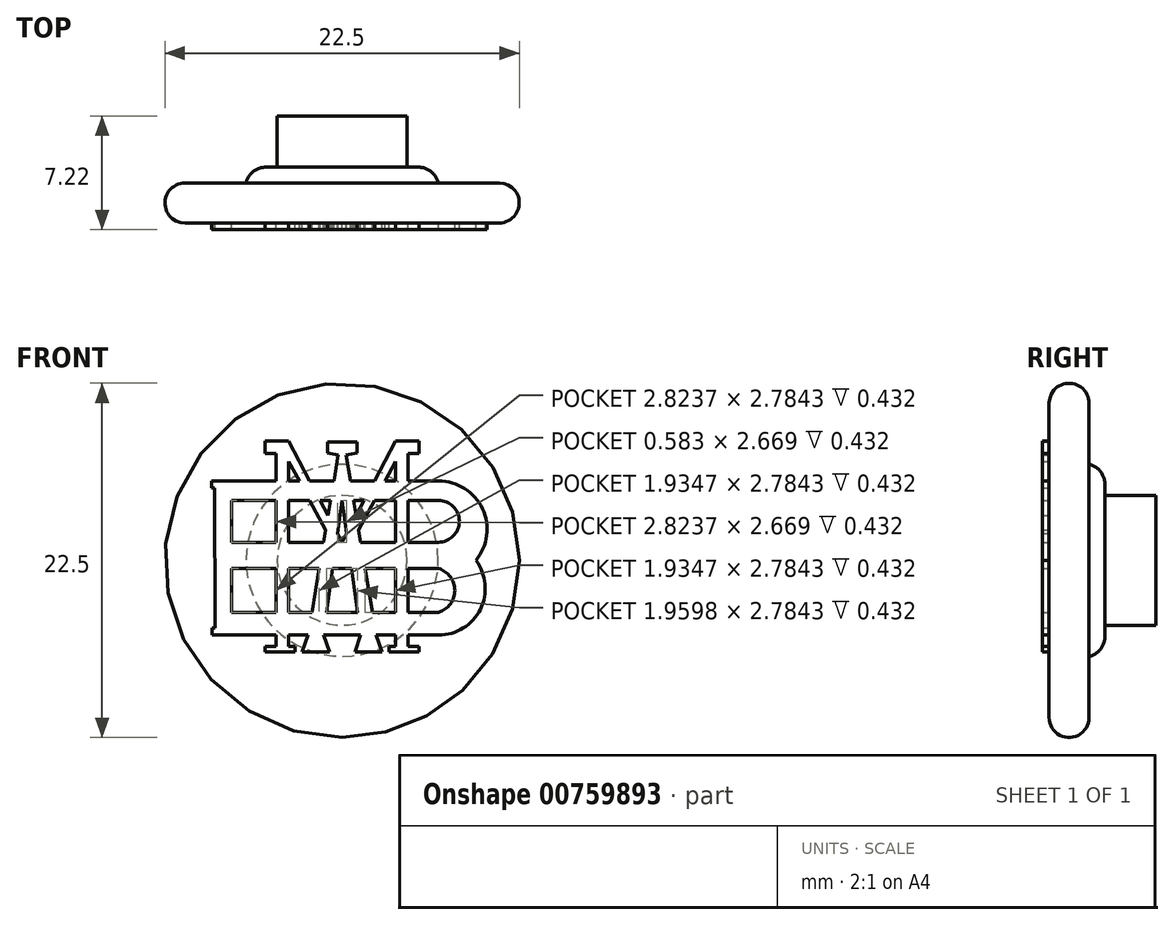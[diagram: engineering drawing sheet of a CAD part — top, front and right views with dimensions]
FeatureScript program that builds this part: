
annotation { "Feature Type Name" : "Feature", "Feature Type Description" : "" }
export const myFeature = defineFeature(function(context is Context, id is Id, definition is map)
    precondition{}
    {
        {
            var Q0;
            Q0=qCreatedBy(makeId("Front.planeOp"),FACE);
            var sketch = newSketch(context, id + "F0", { "sketchPlane" : qUnion([Q0])});
            skCircle(sketch, "E0", {"center": v(0, 0) * mm, "radius": 4.12 * mm});
            skCircle(sketch, "E1", {"center": v(0, 0) * mm, "radius": 11.25 * mm});
            skCircle(sketch, "E2", {"center": v(0, 0) * mm, "radius": 6.1 * mm});
            skSolve(sketch);
        }
        {
            var Q0;
            Q0=makeQuery(id+"F0.imprint","IMPRINT",FACE,{"disambiguationData":[TD([[makeQuery(id+"F0.imprint","IMPRINT",EDGE,{"derivedFrom":sQuery(id+"F0.wireOp",EDGE,"E1")}),1.0]])]});
            var Q1;
            Q1=makeQuery(id+"F0.imprint","IMPRINT",FACE,{"disambiguationData":[TD([[makeQuery(id+"F0.imprint","IMPRINT",EDGE,{"derivedFrom":sQuery(id+"F0.wireOp",EDGE,"E0")}),1.0]])]});
            var Q2;
            Q2=makeQuery(id+"F0.imprint","IMPRINT",FACE,{"disambiguationData":[TD([[makeQuery(id+"F0.imprint","IMPRINT",EDGE,{"derivedFrom":sQuery(id+"F0.wireOp",EDGE,"E0")}),-1.0]])]});
            extrude(context, id + "F1", {"entities" : qUnion([Q0, Q1, Q2]), "depth" : 2.54 * mm, "offsetDistance" : 25.4 * mm});
        }
        {
            var Q0;
            Q0=makeQuery(id+"F0.imprint","IMPRINT",FACE,{"disambiguationData":[TD([[makeQuery(id+"F0.imprint","IMPRINT",EDGE,{"derivedFrom":sQuery(id+"F0.wireOp",EDGE,"E0")}),1.0]])]});
            extrude(context, id + "F2", {"entities" : qUnion([Q0]), "operationType" : NewBodyOperationType.ADD, "oppositeDirection" : true, "depth" : 4.25 * mm, "offsetDistance" : 25.4 * mm});
        }
        {
            var Q0;
            Q0=makeQuery(id+"F0.imprint","IMPRINT",FACE,{"disambiguationData":[TD([[makeQuery(id+"F0.imprint","IMPRINT",EDGE,{"derivedFrom":sQuery(id+"F0.wireOp",EDGE,"E0")}),-1.0]])]});
            extrude(context, id + "F3", {"entities" : qUnion([Q0]), "operationType" : NewBodyOperationType.ADD, "oppositeDirection" : true, "depth" : 1 * mm, "offsetDistance" : 25.4 * mm});
        }
        {
            var Q0;
            Q0=makeQuery(id+"F3.opExtrude","CAP_EDGE",EDGE,{"disambiguationData":[OSD([sQuery(id+"F0.wireOp",EDGE,"E2")])],"isStart":false});
            var Q1;
            Q1=makeQuery(id+"F1.opExtrude","CAP_EDGE",EDGE,{"disambiguationData":[OSD([sQuery(id+"F0.wireOp",EDGE,"E1")])],"isStart":true});
            var Q2;
            Q2=makeQuery(id+"F1.opExtrude","CAP_EDGE",EDGE,{"disambiguationData":[OSD([sQuery(id+"F0.wireOp",EDGE,"E1")])],"isStart":false});
            fillet(context, id + "F4", {"entities" : qUnion([Q0, Q1, Q2]), "radius" : 1.27 * mm, "tangentPropagation" : true, "allowEdgeOverflow" : false});
        }
        {
            var Q0;
            Q0=makeQuery(id+"F1.opExtrude","CAP_FACE",FACE,{"disambiguationData":[OSD([sQuery(id+"F0.wireOp",EDGE,"E1")])],"isStart":false});
            var sketch = newSketch(context, id + "F5", { "sketchPlane" : qUnion([Q0])});
            skArc(sketch, "E3", {"start": v(6.13, 1.14) * mm, "mid": v(7.44, 2.48) * mm, "end": v(6.13, 3.81) * mm});
            skArc(sketch, "E4", {"start": v(6.13, -3.3) * mm, "mid": v(7.15, -1.9) * mm, "end": v(6.13, -0.52) * mm});
            skArc(sketch, "E5", {"start": v(6.13, -4.75) * mm, "mid": v(8.78, -3.1) * mm, "end": v(8.5, 0) * mm});
            skArc(sketch, "E6", {"start": v(8.5, 0) * mm, "mid": v(8.91, 3.27) * mm, "end": v(6.13, 5.04) * mm});
            skLineSegment(sketch, "E7", {"start": v(-2.17, -4.75) * mm, "end": v(-2.54, -5.8) * mm});
            skLineSegment(sketch, "E8", {"start": v(-2.17, -4.75) * mm, "end": v(-0.24, 6.7) * mm});
            skPoint(sketch, "E8.endSnap0", {"position": v(-0.24, 1.14) * mm});
            skLineSegment(sketch, "E9.MirrorCS", {"start": v(2.17, -4.75) * mm, "end": v(0.24, 6.7) * mm});
            skLineSegment(sketch, "E10.MirrorCS", {"start": v(2.17, -4.75) * mm, "end": v(2.54, -5.8) * mm});
            skLineSegment(sketch, "E11", {"start": v(-2.54, -5.8) * mm, "end": v(-0.8, -5.8) * mm});
            skLineSegment(sketch, "E12", {"start": v(-0.8, -5.8) * mm, "end": v(-1.18, -4.75) * mm});
            skLineSegment(sketch, "E13", {"start": v(-0.24, 6.7) * mm, "end": v(-0.93, 6.8) * mm});
            skLineSegment(sketch, "E14", {"start": v(-0.93, 6.8) * mm, "end": v(-0.93, 7.52) * mm});
            skLineSegment(sketch, "E15", {"start": v(-0.93, 7.52) * mm, "end": v(0, 7.52) * mm});
            skLineSegment(sketch, "E16.MirrorCS", {"start": v(0.93, 7.52) * mm, "end": v(0, 7.52) * mm});
            skLineSegment(sketch, "E17.MirrorCS", {"start": v(0.93, 6.8) * mm, "end": v(0.93, 7.52) * mm});
            skLineSegment(sketch, "E18.MirrorCS", {"start": v(0.24, 6.7) * mm, "end": v(0.93, 6.8) * mm});
            skLineSegment(sketch, "E19.MirrorCS", {"start": v(0.8, -5.8) * mm, "end": v(1.18, -4.75) * mm});
            skLineSegment(sketch, "E20.MirrorCS", {"start": v(2.54, -5.8) * mm, "end": v(0.8, -5.8) * mm});
            skLineSegment(sketch, "E21", {"start": v(1.18, -4.75) * mm, "end": v(0, 3.81) * mm});
            skLineSegment(sketch, "E22", {"start": v(-1.18, -4.75) * mm, "end": v(0, 3.81) * mm});
            skLineSegment(sketch, "E23", {"start": v(-4.19, -4.75) * mm, "end": v(-4.19, -5.45) * mm});
            skLineSegment(sketch, "E24", {"start": v(-3.4, -4.75) * mm, "end": v(-3.4, -5.45) * mm});
            skLineSegment(sketch, "E25", {"start": v(-4.19, -4.75) * mm, "end": v(-4.19, 6.79) * mm});
            skLineSegment(sketch, "E26", {"start": v(-4.19, 6.79) * mm, "end": v(-4.88, 6.79) * mm});
            skLineSegment(sketch, "E27", {"start": v(-4.88, 7.58) * mm, "end": v(-3.4, 7.58) * mm});
            skLineSegment(sketch, "E28", {"start": v(-4.88, 7.58) * mm, "end": v(-4.88, 6.79) * mm});
            skLineSegment(sketch, "E29", {"start": v(-3.4, 7.58) * mm, "end": v(0, 1.14) * mm});
            skLineSegment(sketch, "E30", {"start": v(-4.19, -5.45) * mm, "end": v(-4.88, -5.45) * mm});
            skLineSegment(sketch, "E31", {"start": v(-4.88, -5.45) * mm, "end": v(-4.88, -5.8) * mm});
            skLineSegment(sketch, "E32", {"start": v(-4.88, -5.8) * mm, "end": v(-2.98, -5.8) * mm});
            skLineSegment(sketch, "E33", {"start": v(-3.4, -5.45) * mm, "end": v(-2.98, -5.45) * mm});
            skLineSegment(sketch, "E34", {"start": v(-2.98, -5.45) * mm, "end": v(-2.98, -5.8) * mm});
            skLineSegment(sketch, "E35.MirrorCS", {"start": v(3.4, 7.58) * mm, "end": v(0, 1.14) * mm});
            skLineSegment(sketch, "E36.MirrorCS", {"start": v(4.88, 7.58) * mm, "end": v(3.4, 7.58) * mm});
            skLineSegment(sketch, "E37.MirrorCS", {"start": v(4.88, 7.58) * mm, "end": v(4.88, 6.79) * mm});
            skLineSegment(sketch, "E38.MirrorCS", {"start": v(4.19, 6.79) * mm, "end": v(4.88, 6.79) * mm});
            skLineSegment(sketch, "E39.MirrorCS", {"start": v(4.19, -4.75) * mm, "end": v(4.19, 6.79) * mm});
            skLineSegment(sketch, "E40.MirrorCS", {"start": v(4.88, -5.45) * mm, "end": v(4.88, -5.8) * mm});
            skLineSegment(sketch, "E41.MirrorCS", {"start": v(4.19, -5.45) * mm, "end": v(4.88, -5.45) * mm});
            skLineSegment(sketch, "E42.MirrorCS", {"start": v(3.4, -5.45) * mm, "end": v(2.98, -5.45) * mm});
            skLineSegment(sketch, "E43.MirrorCS", {"start": v(2.98, -5.45) * mm, "end": v(2.98, -5.8) * mm});
            skLineSegment(sketch, "E44.MirrorCS", {"start": v(4.88, -5.8) * mm, "end": v(2.98, -5.8) * mm});
            skLineSegment(sketch, "E45.MirrorCS", {"start": v(3.4, -4.75) * mm, "end": v(3.4, -5.45) * mm});
            skLineSegment(sketch, "E46.MirrorCS", {"start": v(4.19, -4.75) * mm, "end": v(4.19, -5.45) * mm});
            skLineSegment(sketch, "E47", {"start": v(-3.4, -4.75) * mm, "end": v(-3.4, 6.3) * mm});
            skLineSegment(sketch, "E48", {"start": v(-3.4, 6.3) * mm, "end": v(0, 0) * mm});
            skLineSegment(sketch, "E49.MirrorCS", {"start": v(3.4, 6.3) * mm, "end": v(0, 0) * mm});
            skLineSegment(sketch, "E50.MirrorCS", {"start": v(3.4, -4.75) * mm, "end": v(3.4, 6.3) * mm});
            skLineSegment(sketch, "E51", {"start": v(6.13, 5.04) * mm, "end": v(5.18, 5.04) * mm});
            skLineSegment(sketch, "E52", {"start": v(-7.71, 5.04) * mm, "end": v(5.18, 5.04) * mm});
            skLineSegment(sketch, "E53", {"start": v(6.13, -4.75) * mm, "end": v(-7.71, -4.75) * mm});
            skLineSegment(sketch, "E54", {"start": v(-7.71, 5.04) * mm, "end": v(-8.3, 5.04) * mm});
            skLineSegment(sketch, "E55", {"start": v(-8.3, 5.04) * mm, "end": v(-8.3, 4.59) * mm});
            skLineSegment(sketch, "E56", {"start": v(-8.3, 4.59) * mm, "end": v(-8.1, 4.59) * mm});
            skLineSegment(sketch, "E57", {"start": v(6.13, 3.81) * mm, "end": v(-7.01, 3.81) * mm});
            skLineSegment(sketch, "E58", {"start": v(6.13, 1.14) * mm, "end": v(-7.01, 1.14) * mm});
            skLineSegment(sketch, "E59", {"start": v(6.13, -0.52) * mm, "end": v(-7.01, -0.52) * mm});
            skLineSegment(sketch, "E60", {"start": v(6.13, -3.3) * mm, "end": v(-7.01, -3.3) * mm});
            skLineSegment(sketch, "E61", {"start": v(-7.01, -3.3) * mm, "end": v(-7.01, 3.81) * mm});
            skLineSegment(sketch, "E62", {"start": v(8.5, 0) * mm, "end": v(-8.1, 0) * mm});
            skLineSegment(sketch, "E63.MirrorCS", {"start": v(-7.68, -4.75) * mm, "end": v(-8.27, -4.75) * mm});
            skLineSegment(sketch, "E64", {"start": v(-8.27, -4.3) * mm, "end": v(-8.27, -4.75) * mm});
            skLineSegment(sketch, "E65", {"start": v(-8.27, -4.3) * mm, "end": v(-8.08, -4.3) * mm});
            skLineSegment(sketch, "E66", {"start": v(-8.1, 4.59) * mm, "end": v(-8.08, -4.3) * mm});
            skSolve(sketch);
        }
        {
            var Q0;
            {var subQ0=sQuery(id+"F5.wireOp",EDGE,"E59");var subQ1=sQuery(id+"F5.wireOp",EDGE,"E25");var subQ2=makeQuery(id+"F5.imprint","INTERSECT",VERTEX,{"derivedFrom":[subQ1,subQ0]});Q0=makeQuery(id+"F5.imprint","IMPRINT",FACE,{"disambiguationData":[TD([[makeQuery(id+"F5.imprint","IMPRINT",EDGE,{"disambiguationData":[TD([[subQ2,-1.0]])],"derivedFrom":subQ1}),1.0]])]});}
            var Q1;
            {var subQ1=sQuery(id+"F5.wireOp",EDGE,"E26");Q1=makeQuery(id+"F5.imprint","IMPRINT",FACE,{"disambiguationData":[TD([[makeQuery(id+"F5.imprint","IMPRINT",EDGE,{"derivedFrom":subQ1}),-1.0]])]});}
            var Q2;
            {var subQ0=sQuery(id+"F5.wireOp",EDGE,"E58");var subQ1=sQuery(id+"F5.wireOp",EDGE,"E22");var subQ2=makeQuery(id+"F5.imprint","INTERSECT",VERTEX,{"derivedFrom":[subQ1,subQ0]});Q2=makeQuery(id+"F5.imprint","IMPRINT",FACE,{"disambiguationData":[TD([[makeQuery(id+"F5.imprint","IMPRINT",EDGE,{"disambiguationData":[TD([[subQ2,-1.0]])],"derivedFrom":subQ1}),-1.0]])]});}
            var Q3;
            {var subQ1=sQuery(id+"F5.wireOp",EDGE,"E36.MirrorCS");Q3=makeQuery(id+"F5.imprint","IMPRINT",FACE,{"disambiguationData":[TD([[makeQuery(id+"F5.imprint","IMPRINT",EDGE,{"derivedFrom":subQ1}),1.0]])]});}
            var Q4;
            {var subQ0=sQuery(id+"F5.wireOp",EDGE,"E13");Q4=makeQuery(id+"F5.imprint","IMPRINT",FACE,{"disambiguationData":[TD([[makeQuery(id+"F5.imprint","IMPRINT",EDGE,{"derivedFrom":subQ0}),-1.0]])]});}
            var Q5;
            {var subQ0=sQuery(id+"F5.wireOp",EDGE,"E58");var subQ1=sQuery(id+"F5.wireOp",EDGE,"E9.MirrorCS");var subQ2=makeQuery(id+"F5.imprint","INTERSECT",VERTEX,{"derivedFrom":[subQ1,subQ0]});Q5=makeQuery(id+"F5.imprint","IMPRINT",FACE,{"disambiguationData":[TD([[makeQuery(id+"F5.imprint","IMPRINT",EDGE,{"disambiguationData":[TD([[subQ2,-1.0]])],"derivedFrom":subQ1}),1.0]])]});}
            var Q6;
            {var subQ0=sQuery(id+"F5.wireOp",EDGE,"E58");var subQ1=sQuery(id+"F5.wireOp",EDGE,"E21");var subQ2=makeQuery(id+"F5.imprint","INTERSECT",VERTEX,{"derivedFrom":[subQ1,subQ0]});Q6=makeQuery(id+"F5.imprint","IMPRINT",FACE,{"disambiguationData":[TD([[makeQuery(id+"F5.imprint","IMPRINT",EDGE,{"disambiguationData":[TD([[subQ2,-1.0]])],"derivedFrom":subQ1}),1.0]])]});}
            var Q7;
            {var subQ14=sQuery(id+"F5.wireOp",EDGE,"E3");Q7=makeQuery(id+"F5.imprint","IMPRINT",FACE,{"disambiguationData":[TD([[makeQuery(id+"F5.imprint","IMPRINT",EDGE,{"derivedFrom":subQ14}),-1.0]])]});}
            var Q8;
            {var subQ1=sQuery(id+"F5.wireOp",EDGE,"E23");Q8=makeQuery(id+"F5.imprint","IMPRINT",FACE,{"disambiguationData":[TD([[makeQuery(id+"F5.imprint","IMPRINT",EDGE,{"derivedFrom":subQ1}),1.0]])]});}
            var Q9;
            {var subQ0=sQuery(id+"F5.wireOp",EDGE,"E7");Q9=makeQuery(id+"F5.imprint","IMPRINT",FACE,{"disambiguationData":[TD([[makeQuery(id+"F5.imprint","IMPRINT",EDGE,{"derivedFrom":subQ0}),1.0]])]});}
            var Q10;
            {var subQ0=sQuery(id+"F5.wireOp",EDGE,"E10.MirrorCS");Q10=makeQuery(id+"F5.imprint","IMPRINT",FACE,{"disambiguationData":[TD([[makeQuery(id+"F5.imprint","IMPRINT",EDGE,{"derivedFrom":subQ0}),-1.0]])]});}
            var Q11;
            Q11=makeQuery(id+"F5.imprint","IMPRINT",FACE,{"disambiguationData":[TD([[makeQuery(id+"F5.imprint","IMPRINT",EDGE,{"derivedFrom":sQuery(id+"F5.wireOp",EDGE,"E40.MirrorCS")}),-1.0]])]});
            var Q12;
            {var subQ0=sQuery(id+"F5.wireOp",EDGE,"E60");var subQ1=sQuery(id+"F5.wireOp",EDGE,"E25");var subQ2=makeQuery(id+"F5.imprint","INTERSECT",VERTEX,{"derivedFrom":[subQ1,subQ0]});Q12=makeQuery(id+"F5.imprint","IMPRINT",FACE,{"disambiguationData":[TD([[makeQuery(id+"F5.imprint","IMPRINT",EDGE,{"disambiguationData":[TD([[subQ2,-1.0]])],"derivedFrom":subQ1}),-1.0]])]});}
            var Q13;
            {var subQ0=sQuery(id+"F5.wireOp",EDGE,"E59");var subQ1=sQuery(id+"F5.wireOp",EDGE,"E25");var subQ2=makeQuery(id+"F5.imprint","INTERSECT",VERTEX,{"derivedFrom":[subQ1,subQ0]});Q13=makeQuery(id+"F5.imprint","IMPRINT",FACE,{"disambiguationData":[TD([[makeQuery(id+"F5.imprint","IMPRINT",EDGE,{"disambiguationData":[TD([[subQ2,-1.0]])],"derivedFrom":subQ1}),-1.0]])]});}
            var Q14;
            {var subQ0=sQuery(id+"F5.wireOp",EDGE,"E58");var subQ1=sQuery(id+"F5.wireOp",EDGE,"E25");var subQ2=makeQuery(id+"F5.imprint","INTERSECT",VERTEX,{"derivedFrom":[subQ1,subQ0]});Q14=makeQuery(id+"F5.imprint","IMPRINT",FACE,{"disambiguationData":[TD([[makeQuery(id+"F5.imprint","IMPRINT",EDGE,{"disambiguationData":[TD([[subQ2,-1.0]])],"derivedFrom":subQ1}),-1.0]])]});}
            var Q15;
            {var subQ0=sQuery(id+"F5.wireOp",EDGE,"E57");var subQ1=sQuery(id+"F5.wireOp",EDGE,"E25");var subQ2=makeQuery(id+"F5.imprint","INTERSECT",VERTEX,{"derivedFrom":[subQ1,subQ0]});Q15=makeQuery(id+"F5.imprint","IMPRINT",FACE,{"disambiguationData":[TD([[makeQuery(id+"F5.imprint","IMPRINT",EDGE,{"disambiguationData":[TD([[subQ2,-1.0]])],"derivedFrom":subQ1}),-1.0]])]});}
            var Q16;
            {var subQ0=sQuery(id+"F5.wireOp",EDGE,"E48");var subQ1=sQuery(id+"F5.wireOp",EDGE,"E8");var subQ2=makeQuery(id+"F5.imprint","INTERSECT",VERTEX,{"derivedFrom":[subQ1,subQ0]});Q16=makeQuery(id+"F5.imprint","IMPRINT",FACE,{"disambiguationData":[TD([[makeQuery(id+"F5.imprint","IMPRINT",EDGE,{"disambiguationData":[TD([[subQ2,-1.0]])],"derivedFrom":subQ1}),-1.0]])]});}
            var Q17;
            {var subQ0=sQuery(id+"F5.wireOp",EDGE,"E48");var subQ1=sQuery(id+"F5.wireOp",EDGE,"E8");var subQ2=makeQuery(id+"F5.imprint","INTERSECT",VERTEX,{"derivedFrom":[subQ1,subQ0]});Q17=makeQuery(id+"F5.imprint","IMPRINT",FACE,{"disambiguationData":[TD([[makeQuery(id+"F5.imprint","IMPRINT",EDGE,{"disambiguationData":[TD([[subQ2,-1.0]])],"derivedFrom":subQ1}),1.0]])]});}
            var Q18;
            {var subQ0=sQuery(id+"F5.wireOp",EDGE,"E29");var subQ1=sQuery(id+"F5.wireOp",EDGE,"E8");var subQ2=makeQuery(id+"F5.imprint","INTERSECT",VERTEX,{"derivedFrom":[subQ1,subQ0]});Q18=makeQuery(id+"F5.imprint","IMPRINT",FACE,{"disambiguationData":[TD([[makeQuery(id+"F5.imprint","IMPRINT",EDGE,{"disambiguationData":[TD([[subQ2,-1.0]])],"derivedFrom":subQ1}),-1.0]])]});}
            var Q19;
            {var subQ0=sQuery(id+"F5.wireOp",EDGE,"E35.MirrorCS");var subQ1=sQuery(id+"F5.wireOp",EDGE,"E9.MirrorCS");var subQ2=makeQuery(id+"F5.imprint","INTERSECT",VERTEX,{"derivedFrom":[subQ1,subQ0]});Q19=makeQuery(id+"F5.imprint","IMPRINT",FACE,{"disambiguationData":[TD([[makeQuery(id+"F5.imprint","IMPRINT",EDGE,{"disambiguationData":[TD([[subQ2,-1.0]])],"derivedFrom":subQ1}),1.0]])]});}
            var Q20;
            {var subQ1=sQuery(id+"F5.wireOp",EDGE,"E9.MirrorCS");var subQ5=sQuery(id+"F5.wireOp",EDGE,"E49.MirrorCS");var subQ6=makeQuery(id+"F5.imprint","INTERSECT",VERTEX,{"derivedFrom":[subQ1,subQ5]});Q20=makeQuery(id+"F5.imprint","IMPRINT",FACE,{"disambiguationData":[TD([[makeQuery(id+"F5.imprint","IMPRINT",EDGE,{"disambiguationData":[TD([[subQ6,-1.0]])],"derivedFrom":subQ1}),1.0]])]});}
            var Q21;
            {var subQ0=sQuery(id+"F5.wireOp",EDGE,"E49.MirrorCS");var subQ3=sQuery(id+"F5.wireOp",EDGE,"E21");var subQ4=makeQuery(id+"F5.imprint","INTERSECT",VERTEX,{"derivedFrom":[subQ3,subQ0]});Q21=makeQuery(id+"F5.imprint","IMPRINT",FACE,{"disambiguationData":[TD([[makeQuery(id+"F5.imprint","IMPRINT",EDGE,{"disambiguationData":[TD([[subQ4,-1.0]])],"derivedFrom":subQ3}),1.0]])]});}
            var Q22;
            {var subQ0=sQuery(id+"F5.wireOp",EDGE,"E60");var subQ1=sQuery(id+"F5.wireOp",EDGE,"E39.MirrorCS");var subQ2=makeQuery(id+"F5.imprint","INTERSECT",VERTEX,{"derivedFrom":[subQ1,subQ0]});Q22=makeQuery(id+"F5.imprint","IMPRINT",FACE,{"disambiguationData":[TD([[makeQuery(id+"F5.imprint","IMPRINT",EDGE,{"disambiguationData":[TD([[subQ2,-1.0]])],"derivedFrom":subQ1}),1.0]])]});}
            var Q23;
            {var subQ0=sQuery(id+"F5.wireOp",EDGE,"E59");var subQ1=sQuery(id+"F5.wireOp",EDGE,"E39.MirrorCS");var subQ2=makeQuery(id+"F5.imprint","INTERSECT",VERTEX,{"derivedFrom":[subQ1,subQ0]});Q23=makeQuery(id+"F5.imprint","IMPRINT",FACE,{"disambiguationData":[TD([[makeQuery(id+"F5.imprint","IMPRINT",EDGE,{"disambiguationData":[TD([[subQ2,-1.0]])],"derivedFrom":subQ1}),1.0]])]});}
            var Q24;
            {var subQ0=sQuery(id+"F5.wireOp",EDGE,"E58");var subQ1=sQuery(id+"F5.wireOp",EDGE,"E39.MirrorCS");var subQ2=makeQuery(id+"F5.imprint","INTERSECT",VERTEX,{"derivedFrom":[subQ1,subQ0]});Q24=makeQuery(id+"F5.imprint","IMPRINT",FACE,{"disambiguationData":[TD([[makeQuery(id+"F5.imprint","IMPRINT",EDGE,{"disambiguationData":[TD([[subQ2,-1.0]])],"derivedFrom":subQ1}),1.0]])]});}
            var Q25;
            {var subQ0=sQuery(id+"F5.wireOp",EDGE,"E57");var subQ1=sQuery(id+"F5.wireOp",EDGE,"E39.MirrorCS");var subQ2=makeQuery(id+"F5.imprint","INTERSECT",VERTEX,{"derivedFrom":[subQ1,subQ0]});Q25=makeQuery(id+"F5.imprint","IMPRINT",FACE,{"disambiguationData":[TD([[makeQuery(id+"F5.imprint","IMPRINT",EDGE,{"disambiguationData":[TD([[subQ2,-1.0]])],"derivedFrom":subQ1}),1.0]])]});}
            var Q26;
            {var subQ0=sQuery(id+"F5.wireOp",EDGE,"E49.MirrorCS");var subQ1=sQuery(id+"F5.wireOp",EDGE,"E9.MirrorCS");var subQ2=makeQuery(id+"F5.imprint","INTERSECT",VERTEX,{"derivedFrom":[subQ1,subQ0]});Q26=makeQuery(id+"F5.imprint","IMPRINT",FACE,{"disambiguationData":[TD([[makeQuery(id+"F5.imprint","IMPRINT",EDGE,{"disambiguationData":[TD([[subQ2,-1.0]])],"derivedFrom":subQ1}),-1.0]])]});}
            var Q27;
            {var subQ0=sQuery(id+"F5.wireOp",EDGE,"E48");var subQ1=sQuery(id+"F5.wireOp",EDGE,"E22");var subQ2=makeQuery(id+"F5.imprint","INTERSECT",VERTEX,{"derivedFrom":[subQ1,subQ0]});Q27=makeQuery(id+"F5.imprint","IMPRINT",FACE,{"disambiguationData":[TD([[makeQuery(id+"F5.imprint","IMPRINT",EDGE,{"disambiguationData":[TD([[subQ2,-1.0]])],"derivedFrom":subQ1}),1.0]])]});}
            var Q28;
            {var subQ0=sQuery(id+"F5.wireOp",EDGE,"E49.MirrorCS");var subQ1=sQuery(id+"F5.wireOp",EDGE,"E21");var subQ2=makeQuery(id+"F5.imprint","INTERSECT",VERTEX,{"derivedFrom":[subQ1,subQ0]});Q28=makeQuery(id+"F5.imprint","IMPRINT",FACE,{"disambiguationData":[TD([[makeQuery(id+"F5.imprint","IMPRINT",EDGE,{"disambiguationData":[TD([[subQ2,-1.0]])],"derivedFrom":subQ1}),-1.0]])]});}
            var Q29;
            {var subQ0=sQuery(id+"F5.wireOp",EDGE,"E52");var subQ1=sQuery(id+"F5.wireOp",EDGE,"E29");var subQ2=makeQuery(id+"F5.imprint","INTERSECT",VERTEX,{"derivedFrom":[subQ1,subQ0]});Q29=makeQuery(id+"F5.imprint","IMPRINT",FACE,{"disambiguationData":[TD([[makeQuery(id+"F5.imprint","IMPRINT",EDGE,{"disambiguationData":[TD([[subQ2,-1.0]])],"derivedFrom":subQ1}),-1.0]])]});}
            var Q30;
            {var subQ0=sQuery(id+"F5.wireOp",EDGE,"E52");var subQ1=sQuery(id+"F5.wireOp",EDGE,"E35.MirrorCS");var subQ2=makeQuery(id+"F5.imprint","INTERSECT",VERTEX,{"derivedFrom":[subQ1,subQ0]});Q30=makeQuery(id+"F5.imprint","IMPRINT",FACE,{"disambiguationData":[TD([[makeQuery(id+"F5.imprint","IMPRINT",EDGE,{"disambiguationData":[TD([[subQ2,-1.0]])],"derivedFrom":subQ1}),1.0]])]});}
            var Q31;
            {var subQ5=sQuery(id+"F5.wireOp",EDGE,"E54");Q31=makeQuery(id+"F5.imprint","IMPRINT",FACE,{"disambiguationData":[TD([[makeQuery(id+"F5.imprint","IMPRINT",EDGE,{"derivedFrom":subQ5}),1.0]])]});}
            var Q32;
            {var subQ0=sQuery(id+"F5.wireOp",EDGE,"E52");var subQ1=sQuery(id+"F5.wireOp",EDGE,"E49.MirrorCS");var subQ2=makeQuery(id+"F5.imprint","INTERSECT",VERTEX,{"derivedFrom":[subQ1,subQ0]});Q32=makeQuery(id+"F5.imprint","IMPRINT",FACE,{"disambiguationData":[TD([[makeQuery(id+"F5.imprint","IMPRINT",EDGE,{"disambiguationData":[TD([[subQ2,-1.0]])],"derivedFrom":subQ1}),1.0]])]});}
            var Q33;
            {var subQ1=sQuery(id+"F5.wireOp",EDGE,"E25");var subQ3=sQuery(id+"F5.wireOp",EDGE,"E60");var subQ4=makeQuery(id+"F5.imprint","INTERSECT",VERTEX,{"derivedFrom":[subQ1,subQ3]});Q33=makeQuery(id+"F5.imprint","IMPRINT",FACE,{"disambiguationData":[TD([[makeQuery(id+"F5.imprint","IMPRINT",EDGE,{"disambiguationData":[TD([[subQ4,1.0]])],"derivedFrom":subQ3}),1.0]])]});}
            var Q34;
            {var subQ0=sQuery(id+"F5.wireOp",EDGE,"E57");var subQ1=sQuery(id+"F5.wireOp",EDGE,"E47");var subQ2=makeQuery(id+"F5.imprint","INTERSECT",VERTEX,{"derivedFrom":[subQ1,subQ0]});Q34=makeQuery(id+"F5.imprint","IMPRINT",FACE,{"disambiguationData":[TD([[makeQuery(id+"F5.imprint","IMPRINT",EDGE,{"disambiguationData":[TD([[subQ2,-1.0]])],"derivedFrom":subQ1}),-1.0]])]});}
            var Q35;
            {var subQ0=sQuery(id+"F5.wireOp",EDGE,"E57");var subQ1=sQuery(id+"F5.wireOp",EDGE,"E8");var subQ2=makeQuery(id+"F5.imprint","INTERSECT",VERTEX,{"derivedFrom":[subQ1,subQ0]});Q35=makeQuery(id+"F5.imprint","IMPRINT",FACE,{"disambiguationData":[TD([[makeQuery(id+"F5.imprint","IMPRINT",EDGE,{"disambiguationData":[TD([[subQ2,-1.0]])],"derivedFrom":subQ1}),1.0]])]});}
            var Q36;
            {var subQ0=sQuery(id+"F5.wireOp",EDGE,"E57");var subQ6=sQuery(id+"F5.wireOp",EDGE,"E8");var subQ8=makeQuery(id+"F5.imprint","INTERSECT",VERTEX,{"derivedFrom":[subQ6,subQ0]});Q36=makeQuery(id+"F5.imprint","IMPRINT",FACE,{"disambiguationData":[TD([[makeQuery(id+"F5.imprint","IMPRINT",EDGE,{"disambiguationData":[TD([[subQ8,-1.0]])],"derivedFrom":subQ6}),-1.0]])]});}
            var Q37;
            {var subQ0=sQuery(id+"F5.wireOp",EDGE,"E57");var subQ1=sQuery(id+"F5.wireOp",EDGE,"E9.MirrorCS");var subQ2=makeQuery(id+"F5.imprint","INTERSECT",VERTEX,{"derivedFrom":[subQ1,subQ0]});Q37=makeQuery(id+"F5.imprint","IMPRINT",FACE,{"disambiguationData":[TD([[makeQuery(id+"F5.imprint","IMPRINT",EDGE,{"disambiguationData":[TD([[subQ2,-1.0]])],"derivedFrom":subQ1}),-1.0]])]});}
            var Q38;
            {var subQ0=sQuery(id+"F5.wireOp",EDGE,"E58");var subQ1=sQuery(id+"F5.wireOp",EDGE,"E8");var subQ2=makeQuery(id+"F5.imprint","INTERSECT",VERTEX,{"derivedFrom":[subQ1,subQ0]});Q38=makeQuery(id+"F5.imprint","IMPRINT",FACE,{"disambiguationData":[TD([[makeQuery(id+"F5.imprint","IMPRINT",EDGE,{"disambiguationData":[TD([[subQ2,-1.0]])],"derivedFrom":subQ1}),-1.0]])]});}
            var Q39;
            {var subQ5=sQuery(id+"F5.wireOp",EDGE,"E9.MirrorCS");var subQ7=sQuery(id+"F5.wireOp",EDGE,"E59");var subQ9=makeQuery(id+"F5.imprint","INTERSECT",VERTEX,{"derivedFrom":[subQ5,subQ7]});Q39=makeQuery(id+"F5.imprint","IMPRINT",FACE,{"disambiguationData":[TD([[makeQuery(id+"F5.imprint","IMPRINT",EDGE,{"disambiguationData":[TD([[subQ9,-1.0]])],"derivedFrom":subQ5}),1.0]])]});}
            var Q40;
            {var subQ0=sQuery(id+"F5.wireOp",EDGE,"E59");var subQ1=sQuery(id+"F5.wireOp",EDGE,"E9.MirrorCS");var subQ2=makeQuery(id+"F5.imprint","INTERSECT",VERTEX,{"derivedFrom":[subQ1,subQ0]});Q40=makeQuery(id+"F5.imprint","IMPRINT",FACE,{"disambiguationData":[TD([[makeQuery(id+"F5.imprint","IMPRINT",EDGE,{"disambiguationData":[TD([[subQ2,-1.0]])],"derivedFrom":subQ1}),-1.0]])]});}
            var Q41;
            {var subQ0=sQuery(id+"F5.wireOp",EDGE,"E59");var subQ1=sQuery(id+"F5.wireOp",EDGE,"E8");var subQ2=makeQuery(id+"F5.imprint","INTERSECT",VERTEX,{"derivedFrom":[subQ1,subQ0]});Q41=makeQuery(id+"F5.imprint","IMPRINT",FACE,{"disambiguationData":[TD([[makeQuery(id+"F5.imprint","IMPRINT",EDGE,{"disambiguationData":[TD([[subQ2,-1.0]])],"derivedFrom":subQ1}),1.0]])]});}
            var Q42;
            {var subQ1=sQuery(id+"F5.wireOp",EDGE,"E8");var subQ7=sQuery(id+"F5.wireOp",EDGE,"E59");var subQ9=makeQuery(id+"F5.imprint","INTERSECT",VERTEX,{"derivedFrom":[subQ1,subQ7]});Q42=makeQuery(id+"F5.imprint","IMPRINT",FACE,{"disambiguationData":[TD([[makeQuery(id+"F5.imprint","IMPRINT",EDGE,{"disambiguationData":[TD([[subQ9,-1.0]])],"derivedFrom":subQ1}),-1.0]])]});}
            var Q43;
            {var subQ0=sQuery(id+"F5.wireOp",EDGE,"E60");var subQ1=sQuery(id+"F5.wireOp",EDGE,"E8");var subQ2=makeQuery(id+"F5.imprint","INTERSECT",VERTEX,{"derivedFrom":[subQ1,subQ0]});Q43=makeQuery(id+"F5.imprint","IMPRINT",FACE,{"disambiguationData":[TD([[makeQuery(id+"F5.imprint","IMPRINT",EDGE,{"disambiguationData":[TD([[subQ2,-1.0]])],"derivedFrom":subQ1}),-1.0]])]});}
            var Q44;
            {var subQ0=sQuery(id+"F5.wireOp",EDGE,"E60");var subQ1=sQuery(id+"F5.wireOp",EDGE,"E9.MirrorCS");var subQ2=makeQuery(id+"F5.imprint","INTERSECT",VERTEX,{"derivedFrom":[subQ1,subQ0]});Q44=makeQuery(id+"F5.imprint","IMPRINT",FACE,{"disambiguationData":[TD([[makeQuery(id+"F5.imprint","IMPRINT",EDGE,{"disambiguationData":[TD([[subQ2,-1.0]])],"derivedFrom":subQ1}),1.0]])]});}
            var Q45;
            {var subQ1=sQuery(id+"F5.wireOp",EDGE,"E9.MirrorCS");var subQ3=sQuery(id+"F5.wireOp",EDGE,"E60");var subQ4=makeQuery(id+"F5.imprint","INTERSECT",VERTEX,{"derivedFrom":[subQ1,subQ3]});Q45=makeQuery(id+"F5.imprint","IMPRINT",FACE,{"disambiguationData":[TD([[makeQuery(id+"F5.imprint","IMPRINT",EDGE,{"disambiguationData":[TD([[subQ4,-1.0]])],"derivedFrom":subQ3}),1.0]])]});}
            var Q46;
            {var subQ1=sQuery(id+"F5.wireOp",EDGE,"E9.MirrorCS");var subQ3=sQuery(id+"F5.wireOp",EDGE,"E60");var subQ4=makeQuery(id+"F5.imprint","INTERSECT",VERTEX,{"derivedFrom":[subQ1,subQ3]});Q46=makeQuery(id+"F5.imprint","IMPRINT",FACE,{"disambiguationData":[TD([[makeQuery(id+"F5.imprint","IMPRINT",EDGE,{"disambiguationData":[TD([[subQ4,1.0]])],"derivedFrom":subQ3}),1.0]])]});}
            var Q47;
            {var subQ1=sQuery(id+"F5.wireOp",EDGE,"E39.MirrorCS");var subQ3=sQuery(id+"F5.wireOp",EDGE,"E60");var subQ4=makeQuery(id+"F5.imprint","INTERSECT",VERTEX,{"derivedFrom":[subQ1,subQ3]});Q47=makeQuery(id+"F5.imprint","IMPRINT",FACE,{"disambiguationData":[TD([[makeQuery(id+"F5.imprint","IMPRINT",EDGE,{"disambiguationData":[TD([[subQ4,-1.0]])],"derivedFrom":subQ3}),1.0]])]});}
            var Q48;
            {var subQ1=sQuery(id+"F5.wireOp",EDGE,"E8");var subQ3=sQuery(id+"F5.wireOp",EDGE,"E60");var subQ4=makeQuery(id+"F5.imprint","INTERSECT",VERTEX,{"derivedFrom":[subQ1,subQ3]});Q48=makeQuery(id+"F5.imprint","IMPRINT",FACE,{"disambiguationData":[TD([[makeQuery(id+"F5.imprint","IMPRINT",EDGE,{"disambiguationData":[TD([[subQ4,1.0]])],"derivedFrom":subQ3}),1.0]])]});}
            var Q49;
            {var subQ1=sQuery(id+"F5.wireOp",EDGE,"E8");var subQ3=sQuery(id+"F5.wireOp",EDGE,"E60");var subQ4=makeQuery(id+"F5.imprint","INTERSECT",VERTEX,{"derivedFrom":[subQ1,subQ3]});Q49=makeQuery(id+"F5.imprint","IMPRINT",FACE,{"disambiguationData":[TD([[makeQuery(id+"F5.imprint","IMPRINT",EDGE,{"disambiguationData":[TD([[subQ4,-1.0]])],"derivedFrom":subQ3}),1.0]])]});}
            var Q50;
            {var subQ1=sQuery(id+"F5.wireOp",EDGE,"E21");var subQ3=sQuery(id+"F5.wireOp",EDGE,"E60");var subQ4=makeQuery(id+"F5.imprint","INTERSECT",VERTEX,{"derivedFrom":[subQ1,subQ3]});Q50=makeQuery(id+"F5.imprint","IMPRINT",FACE,{"disambiguationData":[TD([[makeQuery(id+"F5.imprint","IMPRINT",EDGE,{"disambiguationData":[TD([[subQ4,-1.0]])],"derivedFrom":subQ3}),1.0]])]});}
            var Q51;
            {var subQ3=sQuery(id+"F5.wireOp",EDGE,"E21");var subQ7=sQuery(id+"F5.wireOp",EDGE,"E59");var subQ9=makeQuery(id+"F5.imprint","INTERSECT",VERTEX,{"derivedFrom":[subQ3,subQ7]});Q51=makeQuery(id+"F5.imprint","IMPRINT",FACE,{"disambiguationData":[TD([[makeQuery(id+"F5.imprint","IMPRINT",EDGE,{"disambiguationData":[TD([[subQ9,-1.0]])],"derivedFrom":subQ3}),1.0]])]});}
            var Q52;
            {var subQ0=sQuery(id+"F5.wireOp",EDGE,"E62");var subQ1=sQuery(id+"F5.wireOp",EDGE,"E25");var subQ2=makeQuery(id+"F5.imprint","INTERSECT",VERTEX,{"derivedFrom":[subQ1,subQ0]});Q52=makeQuery(id+"F5.imprint","IMPRINT",FACE,{"disambiguationData":[TD([[makeQuery(id+"F5.imprint","IMPRINT",EDGE,{"disambiguationData":[TD([[subQ2,-1.0]])],"derivedFrom":subQ1}),1.0]])]});}
            var Q53;
            {var subQ0=sQuery(id+"F5.wireOp",EDGE,"E62");var subQ1=sQuery(id+"F5.wireOp",EDGE,"E25");var subQ2=makeQuery(id+"F5.imprint","INTERSECT",VERTEX,{"derivedFrom":[subQ1,subQ0]});Q53=makeQuery(id+"F5.imprint","IMPRINT",FACE,{"disambiguationData":[TD([[makeQuery(id+"F5.imprint","IMPRINT",EDGE,{"disambiguationData":[TD([[subQ2,-1.0]])],"derivedFrom":subQ1}),-1.0]])]});}
            var Q54;
            {var subQ0=sQuery(id+"F5.wireOp",EDGE,"E62");var subQ1=sQuery(id+"F5.wireOp",EDGE,"E8");var subQ2=makeQuery(id+"F5.imprint","INTERSECT",VERTEX,{"derivedFrom":[subQ1,subQ0]});Q54=makeQuery(id+"F5.imprint","IMPRINT",FACE,{"disambiguationData":[TD([[makeQuery(id+"F5.imprint","IMPRINT",EDGE,{"disambiguationData":[TD([[subQ2,-1.0]])],"derivedFrom":subQ1}),1.0]])]});}
            var Q55;
            {var subQ1=sQuery(id+"F5.wireOp",EDGE,"E8");var subQ5=sQuery(id+"F5.wireOp",EDGE,"E62");var subQ6=makeQuery(id+"F5.imprint","INTERSECT",VERTEX,{"derivedFrom":[subQ1,subQ5]});Q55=makeQuery(id+"F5.imprint","IMPRINT",FACE,{"disambiguationData":[TD([[makeQuery(id+"F5.imprint","IMPRINT",EDGE,{"disambiguationData":[TD([[subQ6,-1.0]])],"derivedFrom":subQ1}),-1.0]])]});}
            var Q56;
            {var subQ0=sQuery(id+"F5.wireOp",EDGE,"E62");var subQ1=sQuery(id+"F5.wireOp",EDGE,"E22");var subQ2=makeQuery(id+"F5.imprint","INTERSECT",VERTEX,{"derivedFrom":[subQ1,subQ0]});Q56=makeQuery(id+"F5.imprint","IMPRINT",FACE,{"disambiguationData":[TD([[makeQuery(id+"F5.imprint","IMPRINT",EDGE,{"disambiguationData":[TD([[subQ2,-1.0]])],"derivedFrom":subQ1}),-1.0]])]});}
            var Q57;
            {var subQ0=sQuery(id+"F5.wireOp",EDGE,"E62");var subQ1=sQuery(id+"F5.wireOp",EDGE,"E21");var subQ2=makeQuery(id+"F5.imprint","INTERSECT",VERTEX,{"derivedFrom":[subQ1,subQ0]});Q57=makeQuery(id+"F5.imprint","IMPRINT",FACE,{"disambiguationData":[TD([[makeQuery(id+"F5.imprint","IMPRINT",EDGE,{"disambiguationData":[TD([[subQ2,-1.0]])],"derivedFrom":subQ1}),1.0]])]});}
            var Q58;
            {var subQ5=sQuery(id+"F5.wireOp",EDGE,"E9.MirrorCS");var subQ7=sQuery(id+"F5.wireOp",EDGE,"E62");var subQ9=makeQuery(id+"F5.imprint","INTERSECT",VERTEX,{"derivedFrom":[subQ5,subQ7]});Q58=makeQuery(id+"F5.imprint","IMPRINT",FACE,{"disambiguationData":[TD([[makeQuery(id+"F5.imprint","IMPRINT",EDGE,{"disambiguationData":[TD([[subQ9,-1.0]])],"derivedFrom":subQ5}),1.0]])]});}
            var Q59;
            {var subQ0=sQuery(id+"F5.wireOp",EDGE,"E62");var subQ1=sQuery(id+"F5.wireOp",EDGE,"E9.MirrorCS");var subQ2=makeQuery(id+"F5.imprint","INTERSECT",VERTEX,{"derivedFrom":[subQ1,subQ0]});Q59=makeQuery(id+"F5.imprint","IMPRINT",FACE,{"disambiguationData":[TD([[makeQuery(id+"F5.imprint","IMPRINT",EDGE,{"disambiguationData":[TD([[subQ2,-1.0]])],"derivedFrom":subQ1}),-1.0]])]});}
            var Q60;
            {var subQ0=sQuery(id+"F5.wireOp",EDGE,"E62");var subQ1=sQuery(id+"F5.wireOp",EDGE,"E39.MirrorCS");var subQ2=makeQuery(id+"F5.imprint","INTERSECT",VERTEX,{"derivedFrom":[subQ1,subQ0]});Q60=makeQuery(id+"F5.imprint","IMPRINT",FACE,{"disambiguationData":[TD([[makeQuery(id+"F5.imprint","IMPRINT",EDGE,{"disambiguationData":[TD([[subQ2,-1.0]])],"derivedFrom":subQ1}),1.0]])]});}
            var Q61;
            {var subQ9=sQuery(id+"F5.wireOp",EDGE,"E4");Q61=makeQuery(id+"F5.imprint","IMPRINT",FACE,{"disambiguationData":[TD([[makeQuery(id+"F5.imprint","IMPRINT",EDGE,{"derivedFrom":subQ9}),-1.0]])]});}
            var Q62;
            {var subQ1=sQuery(id+"F5.wireOp",EDGE,"E64");Q62=makeQuery(id+"F5.imprint","IMPRINT",FACE,{"disambiguationData":[TD([[makeQuery(id+"F5.imprint","IMPRINT",EDGE,{"derivedFrom":subQ1}),1.0]])]});}
            extrude(context, id + "F6", {"entities" : qUnion([Q0, Q1, Q2, Q3, Q4, Q5, Q6, Q7, Q8, Q9, Q10, Q11, Q12, Q13, Q14, Q15, Q16, Q17, Q18, Q19, Q20, Q21, Q22, Q23, Q24, Q25, Q26, Q27, Q28, Q29, Q30, Q31, Q32, Q33, Q34, Q35, Q36, Q37, Q38, Q39, Q40, Q41, Q42, Q43, Q44, Q45, Q46, Q47, Q48, Q49, Q50, Q51, Q52, Q53, Q54, Q55, Q56, Q57, Q58, Q59, Q60, Q61, Q62]), "operationType" : NewBodyOperationType.ADD, "depth" : 0.43 * mm, "offsetDistance" : 25.4 * mm});
        }
    });
